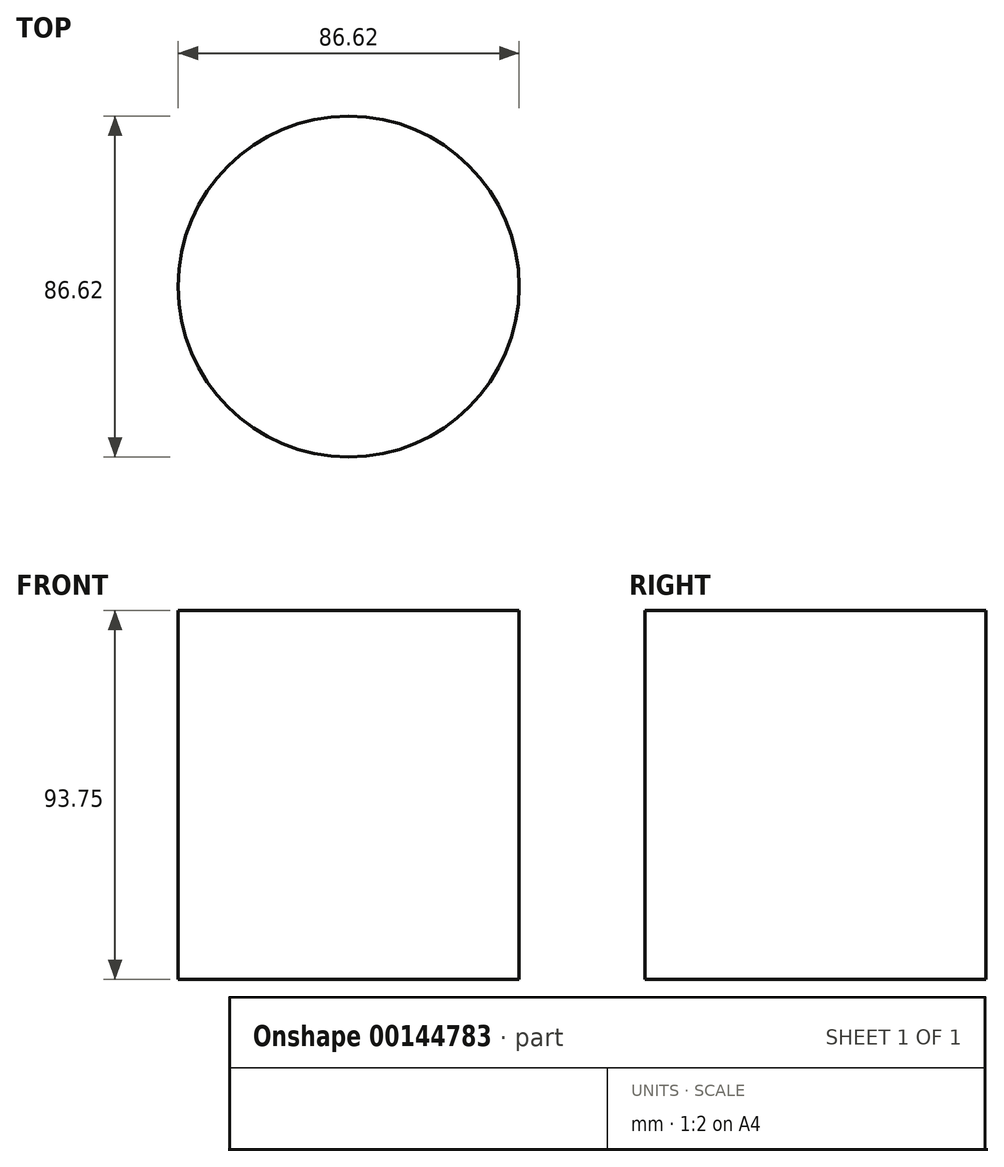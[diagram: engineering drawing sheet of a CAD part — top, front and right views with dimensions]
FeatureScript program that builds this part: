
annotation { "Feature Type Name" : "Feature", "Feature Type Description" : "" }
export const myFeature = defineFeature(function(context is Context, id is Id, definition is map)
    precondition{}
    {
        {
            var Q0;
            Q0=qCreatedBy(makeId("Top.planeOp"),FACE);
            var sketch = newSketch(context, id + "F0", { "sketchPlane" : qUnion([Q0])});
            skCircle(sketch, "E0", {"center": v(0, 0) * mm, "radius": 43.31 * mm});
            skSolve(sketch);
        }
        {
            var Q0;
            Q0 = qSketchRegion(id + "F0", true);
            extrude(context, id + "F1", {"entities" : qUnion([Q0]), "depth" : 93.75 * mm});
        }
    });
